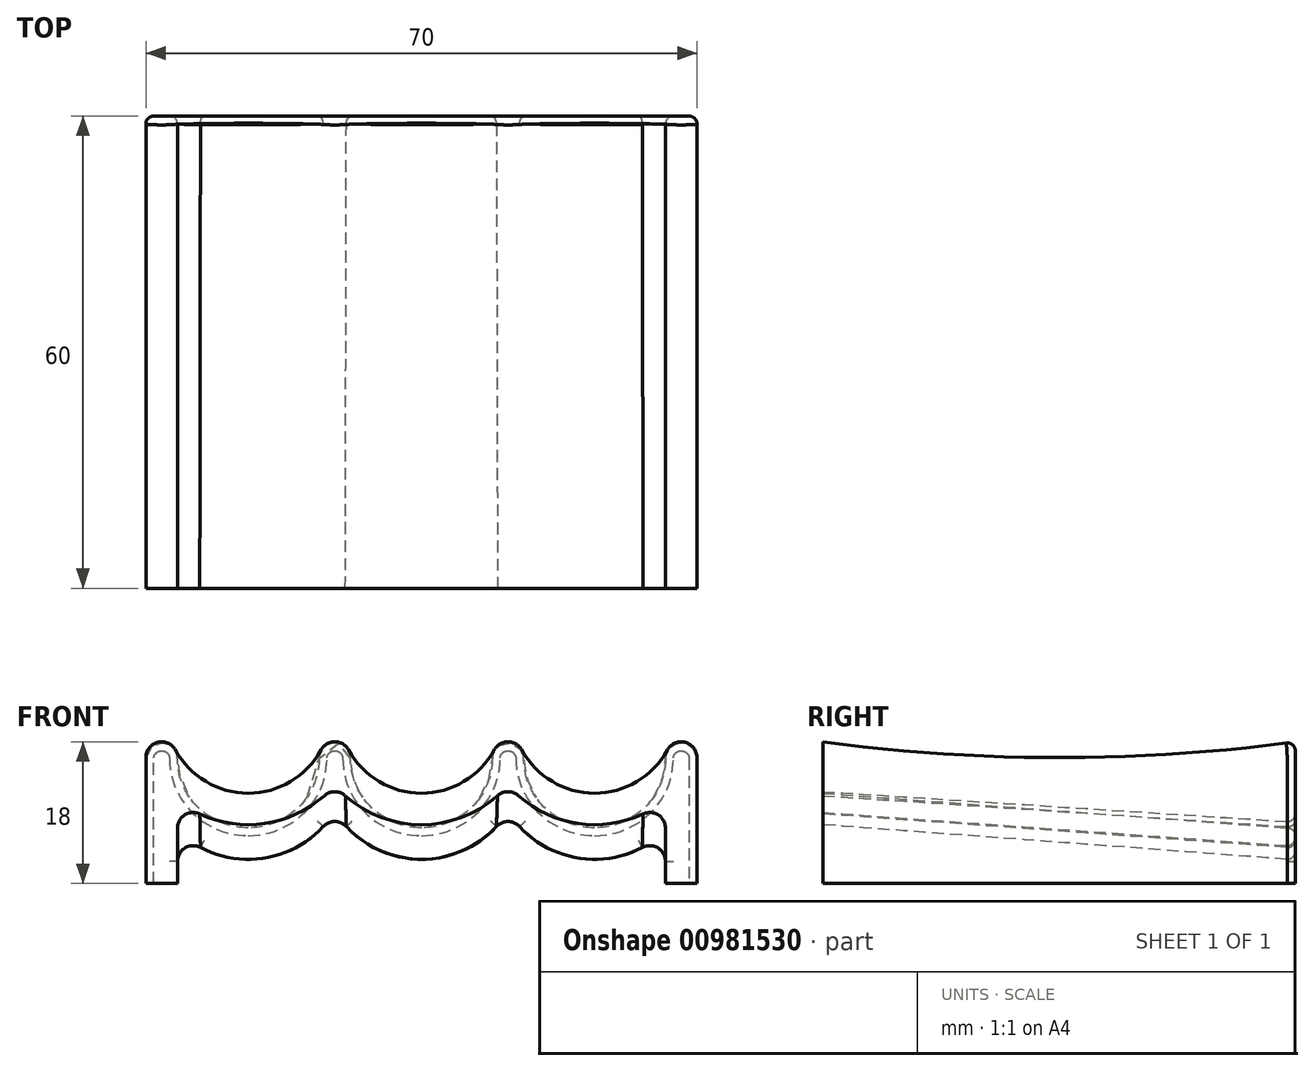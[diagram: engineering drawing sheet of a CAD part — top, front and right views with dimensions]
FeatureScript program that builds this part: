
annotation { "Feature Type Name" : "Feature", "Feature Type Description" : "" }
export const myFeature = defineFeature(function(context is Context, id is Id, definition is map)
    precondition{}
    {
        {
            var Q0;
            Q0=qCreatedBy(makeId("Front.planeOp"),FACE);
            var sketch = newSketch(context, id + "F0", { "sketchPlane" : qUnion([Q0])});
            skArc(sketch, "E0", {"start": v(-31, 16) * mm, "mid": v(-22, 7) * mm, "end": v(-13, 16) * mm});
            skArc(sketch, "E1", {"start": v(-9, 16) * mm, "mid": v(-11, 18) * mm, "end": v(-13, 16) * mm});
            skArc(sketch, "E2", {"start": v(-31, 16) * mm, "mid": v(-33, 18) * mm, "end": v(-35, 16) * mm});
            skArc(sketch, "E3", {"start": v(-9, 16) * mm, "mid": v(0, 7) * mm, "end": v(9, 16) * mm});
            skArc(sketch, "E4", {"start": v(13, 16) * mm, "mid": v(11, 18) * mm, "end": v(9, 16) * mm});
            skArc(sketch, "E5", {"start": v(13, 16) * mm, "mid": v(22, 7) * mm, "end": v(31, 16) * mm});
            skArc(sketch, "E6", {"start": v(35, 16) * mm, "mid": v(33, 18) * mm, "end": v(31, 16) * mm});
            skArc(sketch, "E7.0", {"start": v(11, 9.07) * mm, "mid": v(20.42, 3.1) * mm, "end": v(31, 6.62) * mm});
            skArc(sketch, "E7.1", {"start": v(-11, 9.07) * mm, "mid": v(0, 3) * mm, "end": v(11, 9.07) * mm});
            skArc(sketch, "E7.2", {"start": v(-31, 6.62) * mm, "mid": v(-20.42, 3.1) * mm, "end": v(-11, 9.07) * mm});
            skLineSegment(sketch, "E8", {"start": v(-35, 16) * mm, "end": v(-35, 0) * mm});
            skLineSegment(sketch, "E9", {"start": v(-35, 0) * mm, "end": v(-31, 0) * mm});
            skLineSegment(sketch, "E10", {"start": v(-31, 0) * mm, "end": v(-31, 6.62) * mm});
            skLineSegment(sketch, "E11", {"start": v(35, 16) * mm, "end": v(35, 0) * mm});
            skLineSegment(sketch, "E12", {"start": v(35, 0) * mm, "end": v(31, 0) * mm});
            skLineSegment(sketch, "E13", {"start": v(31, 0) * mm, "end": v(31, 6.62) * mm});
            skSolve(sketch);
        }
        {
            var Q0;
            Q0=qCreatedBy(makeId("Front.planeOp"),FACE);
            cPlane(context, id + "F1", {"entities" : qUnion([Q0]), "cplaneType" : CPlaneType.OFFSET, "offset" : 60 * mm, "width" : 150 * mm, "height" : 150 * mm});
        }
        {
            var Q0;
            Q0=qCreatedBy(id+"F1.planeOp",FACE);
            var sketch = newSketch(context, id + "F2", { "sketchPlane" : qUnion([Q0])});
            skArc(sketch, "E14", {"start": v(-31.24, 16.96) * mm, "mid": v(-22, 11.47) * mm, "end": v(-12.76, 16.96) * mm});
            skArc(sketch, "E15", {"start": v(-31.24, 16.96) * mm, "mid": v(-33.5, 17.94) * mm, "end": v(-35, 16) * mm});
            skArc(sketch, "E16", {"start": v(-9.24, 16.96) * mm, "mid": v(-11, 18) * mm, "end": v(-12.76, 16.96) * mm});
            skArc(sketch, "E17", {"start": v(-9.24, 16.96) * mm, "mid": v(0, 11.47) * mm, "end": v(9.24, 16.96) * mm});
            skArc(sketch, "E18", {"start": v(12.76, 16.96) * mm, "mid": v(11, 18) * mm, "end": v(9.24, 16.96) * mm});
            skArc(sketch, "E19", {"start": v(12.76, 16.96) * mm, "mid": v(22, 11.47) * mm, "end": v(31.24, 16.96) * mm});
            skArc(sketch, "E20", {"start": v(35, 16) * mm, "mid": v(33.5, 17.94) * mm, "end": v(31.24, 16.96) * mm});
            skArc(sketch, "E21.0", {"start": v(11, 12.5) * mm, "mid": v(20.62, 7.54) * mm, "end": v(31, 10.6) * mm});
            skArc(sketch, "E21.1", {"start": v(-11, 12.5) * mm, "mid": v(0, 7.47) * mm, "end": v(11, 12.5) * mm});
            skArc(sketch, "E21.2", {"start": v(-31, 10.6) * mm, "mid": v(-20.62, 7.54) * mm, "end": v(-11, 12.5) * mm});
            skLineSegment(sketch, "E22", {"start": v(-35, 16) * mm, "end": v(-35, 0) * mm});
            skLineSegment(sketch, "E23", {"start": v(-35, 0) * mm, "end": v(-31, 0) * mm});
            skLineSegment(sketch, "E24", {"start": v(-31, 0) * mm, "end": v(-31, 10.6) * mm});
            skLineSegment(sketch, "E25", {"start": v(31, 0) * mm, "end": v(35, 0) * mm});
            skLineSegment(sketch, "E26", {"start": v(35, 0) * mm, "end": v(35, 16) * mm});
            skLineSegment(sketch, "E27", {"start": v(31, 0) * mm, "end": v(31, 10.6) * mm});
            skArc(sketch, "E28.0", {"start": v(-31, 16) * mm, "mid": v(-33, 18) * mm, "end": v(-35, 16) * mm, "construction": true});
            skArc(sketch, "E29.0", {"start": v(-9, 16) * mm, "mid": v(-11, 18) * mm, "end": v(-13, 16) * mm, "construction": true});
            skPoint(sketch, "E30.0", {"position": v(-22, 16) * mm});
            skLineSegment(sketch, "E31", {"start": v(-11, 14) * mm, "end": v(-33, 14) * mm, "construction": true});
            skSolve(sketch);
        }
        {
            var Q0;
            Q0=sQuery(id+"F0.wireOp",EDGE,"E4");
            cPlane(context, id + "F3", {"entities" : qUnion([Q0]), "cplaneType" : CPlaneType.LINE_ANGLE, "offset" : 25 * mm, "angle" : 90 * degree, "width" : 150 * mm, "height" : 150 * mm});
        }
        {
            var Q0;
            Q0=qCreatedBy(id+"F3.planeOp",FACE);
            var sketch = newSketch(context, id + "F4", { "sketchPlane" : qUnion([Q0])});
            skPoint(sketch, "E32.0", {"position": v(0, 18) * mm});
            skPoint(sketch, "E33.0", {"position": v(-60, 18) * mm});
            skLineSegment(sketch, "E34", {"start": v(0, 18) * mm, "end": v(-60, 18) * mm, "construction": true});
            skArc(sketch, "E35", {"start": v(-60, 18) * mm, "mid": v(-30, 16) * mm, "end": v(0, 18) * mm});
            skPoint(sketch, "E36.0", {"position": v(0, 9.07) * mm});
            skPoint(sketch, "E37.0", {"position": v(-60, 12.5) * mm});
            skLineSegment(sketch, "E38", {"start": v(0, 9.07) * mm, "end": v(-60, 12.5) * mm});
            skSolve(sketch);
        }
        {
            var Q0;
            Q0=sQuery(id+"F0.wireOp",EDGE,"E2");
            cPlane(context, id + "F5", {"entities" : qUnion([Q0]), "cplaneType" : CPlaneType.LINE_ANGLE, "offset" : 25 * mm, "angle" : 90 * degree, "width" : 150 * mm, "height" : 150 * mm});
        }
        {
            var Q0;
            Q0=qCreatedBy(id+"F5.planeOp",FACE);
            var sketch = newSketch(context, id + "F6", { "sketchPlane" : qUnion([Q0])});
            skArc(sketch, "E39.0", {"start": v(-60, 18) * mm, "mid": v(-30, 16) * mm, "end": v(0, 18) * mm});
            skSolve(sketch);
        }
        {
            var Q0;
            Q0=sQuery(id+"F0.wireOp",EDGE,"E1");
            cPlane(context, id + "F7", {"entities" : qUnion([Q0]), "cplaneType" : CPlaneType.LINE_ANGLE, "offset" : 25 * mm, "angle" : 90 * degree, "width" : 150 * mm, "height" : 150 * mm});
        }
        {
            var Q0;
            Q0=qCreatedBy(id+"F7.planeOp",FACE);
            var sketch = newSketch(context, id + "F8", { "sketchPlane" : qUnion([Q0])});
            skArc(sketch, "E40.0", {"start": v(-60, 18) * mm, "mid": v(-30, 16) * mm, "end": v(0, 18) * mm});
            skLineSegment(sketch, "E41.0", {"start": v(0, 9.07) * mm, "end": v(-60, 12.5) * mm});
            skSolve(sketch);
        }
        {
            var Q0;
            Q0=sQuery(id+"F0.wireOp",EDGE,"E6");
            cPlane(context, id + "F9", {"entities" : qUnion([Q0]), "cplaneType" : CPlaneType.LINE_ANGLE, "offset" : 25 * mm, "angle" : 90 * degree, "width" : 150 * mm, "height" : 150 * mm});
        }
        {
            var Q0;
            Q0=qCreatedBy(id+"F9.planeOp",FACE);
            var sketch = newSketch(context, id + "F10", { "sketchPlane" : qUnion([Q0])});
            skArc(sketch, "E42.0", {"start": v(-60, 18) * mm, "mid": v(-30, 16) * mm, "end": v(0, 18) * mm});
            skSolve(sketch);
        }
        {
            var Q0;
            Q0=sQuery(id+"F2.wireOp",EDGE,"E19");
            cPlane(context, id + "F11", {"entities" : qUnion([Q0]), "cplaneType" : CPlaneType.LINE_ANGLE, "offset" : 25 * mm, "angle" : 90 * degree, "width" : 150 * mm, "height" : 150 * mm});
        }
        {
            var Q0;
            Q0=qCreatedBy(id+"F11.planeOp",FACE);
            var sketch = newSketch(context, id + "F12", { "sketchPlane" : qUnion([Q0])});
            skPoint(sketch, "E43.0", {"position": v(-60, 11.47) * mm});
            skPoint(sketch, "E44.0", {"position": v(0, 7) * mm});
            skLineSegment(sketch, "E45", {"start": v(-60, 11.47) * mm, "end": v(0, 7) * mm});
            skSolve(sketch);
        }
        {
            var Q0;
            Q0=sQuery(id+"F2.wireOp",EDGE,"E17");
            cPlane(context, id + "F13", {"entities" : qUnion([Q0]), "cplaneType" : CPlaneType.LINE_ANGLE, "offset" : 25 * mm, "angle" : 90 * degree, "width" : 150 * mm, "height" : 150 * mm});
        }
        {
            var Q0;
            Q0=qCreatedBy(id+"F13.planeOp",FACE);
            var sketch = newSketch(context, id + "F14", { "sketchPlane" : qUnion([Q0])});
            skLineSegment(sketch, "E46.0", {"start": v(-60, 11.47) * mm, "end": v(0, 7) * mm});
            skSolve(sketch);
        }
        {
            var Q0;
            Q0=sQuery(id+"F2.wireOp",EDGE,"E14");
            cPlane(context, id + "F15", {"entities" : qUnion([Q0]), "cplaneType" : CPlaneType.LINE_ANGLE, "offset" : 25 * mm, "angle" : 90 * degree, "width" : 150 * mm, "height" : 150 * mm});
        }
        {
            var Q0;
            Q0=qCreatedBy(id+"F15.planeOp",FACE);
            var sketch = newSketch(context, id + "F16", { "sketchPlane" : qUnion([Q0])});
            skLineSegment(sketch, "E47.0", {"start": v(-60, 11.47) * mm, "end": v(0, 7) * mm});
            skSolve(sketch);
        }
        {
            var Q0;
            Q0 = qSketchRegion(id + "F0", true);
            var Q1;
            Q1 = qSketchRegion(id + "F2", true);
            var Q2;
            Q2=sQuery(id+"F10.wireOp",EDGE,"E42.0");
            var Q3;
            Q3=sQuery(id+"F4.wireOp",EDGE,"E35");
            var Q4;
            Q4=sQuery(id+"F4.wireOp",EDGE,"E38");
            var Q5;
            Q5=sQuery(id+"F8.wireOp",EDGE,"E40.0");
            var Q6;
            Q6=sQuery(id+"F8.wireOp",EDGE,"E41.0");
            var Q7;
            Q7=sQuery(id+"F6.wireOp",EDGE,"E39.0");
            var Q8;
            Q8=sQuery(id+"F12.wireOp",EDGE,"E45");
            var Q9;
            Q9=sQuery(id+"F14.wireOp",EDGE,"E46.0");
            var Q10;
            Q10=sQuery(id+"F16.wireOp",EDGE,"E47.0");
            loft(context, id + "F17", {"addGuides" : true, "sheetProfilesArray" : [{ "sheetProfileEntities" : qUnion([Q0]) }, { "sheetProfileEntities" : qUnion([Q1]) }], "guidesArray" : [{ "guideEntities" : qUnion([Q2]), "guideDerivativeType" : LoftGuideDerivativeType.DEFAULT, "guideDerivativeMagnitude" : 1 }, { "guideEntities" : qUnion([Q3]), "guideDerivativeType" : LoftGuideDerivativeType.DEFAULT, "guideDerivativeMagnitude" : 1 }, { "guideEntities" : qUnion([Q4]), "guideDerivativeType" : LoftGuideDerivativeType.DEFAULT, "guideDerivativeMagnitude" : 1 }, { "guideEntities" : qUnion([Q5]), "guideDerivativeType" : LoftGuideDerivativeType.DEFAULT, "guideDerivativeMagnitude" : 1 }, { "guideEntities" : qUnion([Q6]), "guideDerivativeType" : LoftGuideDerivativeType.DEFAULT, "guideDerivativeMagnitude" : 1 }, { "guideEntities" : qUnion([Q7]), "guideDerivativeType" : LoftGuideDerivativeType.DEFAULT, "guideDerivativeMagnitude" : 1 }, { "guideEntities" : qUnion([Q8]), "guideDerivativeType" : LoftGuideDerivativeType.DEFAULT, "guideDerivativeMagnitude" : 1 }, { "guideEntities" : qUnion([Q9]), "guideDerivativeType" : LoftGuideDerivativeType.DEFAULT, "guideDerivativeMagnitude" : 1 }, { "guideEntities" : qUnion([Q10]), "guideDerivativeType" : LoftGuideDerivativeType.DEFAULT, "guideDerivativeMagnitude" : 1 }]});
        }
        {
            var Q0;
            Q0=makeQuery(id+"F17.opLoft","SWEPT_EDGE",EDGE,{"disambiguationData":[OSD([sQuery(id+"F0.wireOp",EDGE,"E7.1"),sQuery(id+"F0.wireOp",EDGE,"E7.2"),sQuery(id+"F2.wireOp",EDGE,"E21.1"),sQuery(id+"F2.wireOp",EDGE,"E21.2"),sQuery(id+"F8.wireOp",EDGE,"E41.0")])]});
            var Q1;
            Q1=makeQuery(id+"F17.opLoft","SWEPT_EDGE",EDGE,{"disambiguationData":[OSD([sQuery(id+"F0.wireOp",EDGE,"E7.0"),sQuery(id+"F0.wireOp",EDGE,"E7.1"),sQuery(id+"F2.wireOp",EDGE,"E21.0"),sQuery(id+"F2.wireOp",EDGE,"E21.1"),sQuery(id+"F4.wireOp",EDGE,"E38")])]});
            var Q2;
            Q2=makeQuery(id+"F17.opLoft","SWEPT_EDGE",EDGE,{"disambiguationData":[OSD([sQuery(id+"F0.wireOp",EDGE,"E7.0"),sQuery(id+"F0.wireOp",EDGE,"E13"),sQuery(id+"F2.wireOp",EDGE,"E21.0"),sQuery(id+"F2.wireOp",EDGE,"E27")])]});
            var Q3;
            Q3=makeQuery(id+"F17.opLoft","SWEPT_EDGE",EDGE,{"disambiguationData":[OSD([sQuery(id+"F0.wireOp",EDGE,"E7.2"),sQuery(id+"F0.wireOp",EDGE,"E10"),sQuery(id+"F2.wireOp",EDGE,"E21.2"),sQuery(id+"F2.wireOp",EDGE,"E24")])]});
            fillet(context, id + "F18", {"entities" : qUnion([Q0, Q1, Q2, Q3]), "radius" : 2 * mm, "tangentPropagation" : true, "allowEdgeOverflow" : false});
        }
        {
            var Q0;
            Q0=makeQuery(id+"F17.opLoft","MID_CAP_EDGE",EDGE,{"disambiguationData":[OSD([sQuery(id+"F0.wireOp",EDGE,"E4"),sQuery(id+"F0.wireOp",EDGE,"E5"),sQuery(id+"F12.wireOp",EDGE,"E45")])],"capPos":0.0});
            var Q1;
            Q1=makeQuery(id+"F17.opLoft","MID_CAP_EDGE",EDGE,{"disambiguationData":[OSD([sQuery(id+"F0.wireOp",EDGE,"E5"),sQuery(id+"F0.wireOp",EDGE,"E6"),sQuery(id+"F12.wireOp",EDGE,"E45")])],"capPos":0.0});
            var Q2;
            {var subQ0=sQuery(id+"F0.wireOp",EDGE,"E7.0");var subQ1=sQuery(id+"F0.wireOp",EDGE,"E13");Q2=makeQuery(id+"F18.opFillet","BLEND_EDGE",EDGE,{"blendedFrom":[makeQuery(id+"F17.opLoft","SWEPT_EDGE",EDGE,{"disambiguationData":[OSD([subQ0,subQ1,sQuery(id+"F2.wireOp",EDGE,"E21.0"),sQuery(id+"F2.wireOp",EDGE,"E27")])]}),makeQuery(id+"F17.opLoft","CAP_FACE",FACE,{"disambiguationData":[OSD([makeQuery(id+"F0.imprint","IMPRINT",FACE,{"disambiguationData":[TD([[makeQuery(id+"F0.imprint","IMPRINT",EDGE,{"derivedFrom":sQuery(id+"F0.wireOp",EDGE,"E0")}),-1.0]])]})])],"isStart":true})],"blendedInto":[makeQuery(id+"F17.opLoft","CAP_FACE",FACE,{"disambiguationData":[OSD([makeQuery(id+"F0.imprint","IMPRINT",FACE,{"disambiguationData":[TD([[makeQuery(id+"F0.imprint","IMPRINT",EDGE,{"derivedFrom":sQuery(id+"F0.wireOp",EDGE,"E0")}),-1.0]])]})])],"isStart":true})]});}
            fillet(context, id + "F19", {"entities" : qUnion([Q0, Q1, Q2]), "radius" : 1 * mm, "tangentPropagation" : true, "allowEdgeOverflow" : false});
        }
    });
